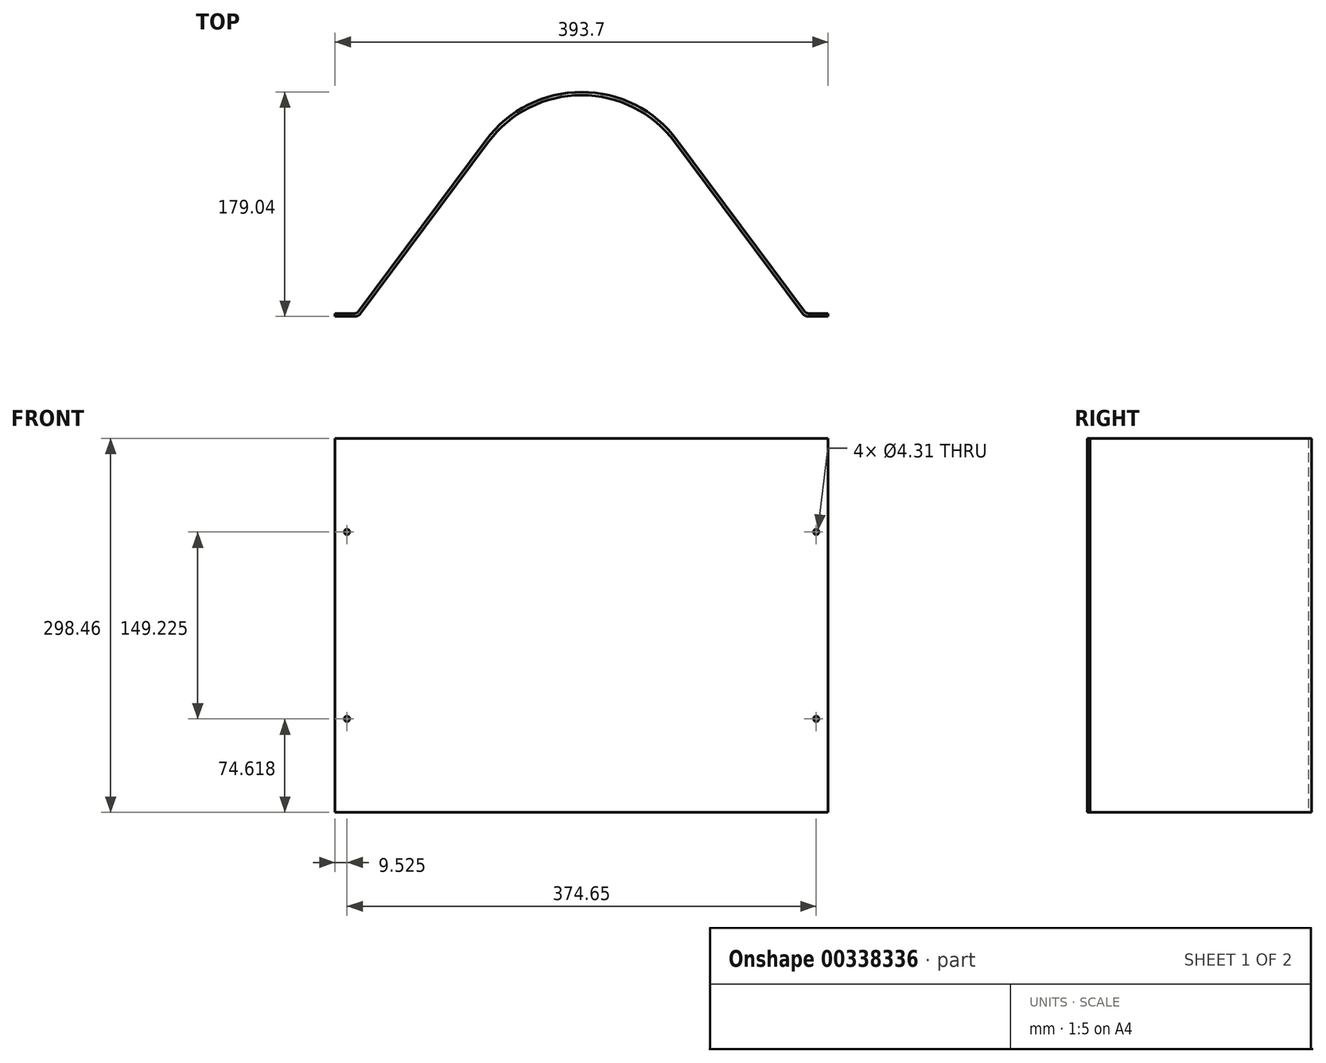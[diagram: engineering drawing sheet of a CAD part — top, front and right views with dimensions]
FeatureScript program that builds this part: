
annotation { "Feature Type Name" : "Feature", "Feature Type Description" : "" }
export const myFeature = defineFeature(function(context is Context, id is Id, definition is map)
    precondition{}
    {
        {
            var Q0;
            Q0=qCreatedBy(makeId("Top.planeOp"),FACE);
            var sketch = newSketch(context, id + "F0", { "sketchPlane" : qUnion([Q0])});
            skLineSegment(sketch, "E0", {"start": v(0, 0) * mm, "end": v(15.88, 0) * mm});
            skLineSegment(sketch, "E1", {"start": v(0, 0) * mm, "end": v(0, -2.38) * mm});
            skLineSegment(sketch, "E2", {"start": v(0, -2.38) * mm, "end": v(393.7, -2.38) * mm});
            skArc(sketch, "E3", {"start": v(15.88, 0) * mm, "mid": v(17.3, 0.34) * mm, "end": v(18.42, 1.28) * mm});
            skLineSegment(sketch, "E4", {"start": v(393.7, -2.38) * mm, "end": v(393.7, 0) * mm});
            skLineSegment(sketch, "E5", {"start": v(393.7, 0) * mm, "end": v(377.83, 0) * mm});
            skLineSegment(sketch, "E6", {"start": v(196.85, -2.38) * mm, "end": v(196.85, 81.57) * mm, "construction": true});
            skArc(sketch, "E7", {"start": v(375.28, 1.28) * mm, "mid": v(376.4, 0.34) * mm, "end": v(377.83, 0) * mm});
            skArc(sketch, "E8", {"start": v(273.1, 138.39) * mm, "mid": v(196.85, 176.66) * mm, "end": v(120.6, 138.39) * mm});
            skLineSegment(sketch, "E9", {"start": v(273.1, 138.39) * mm, "end": v(375.28, 1.28) * mm});
            skLineSegment(sketch, "E10", {"start": v(120.6, 138.39) * mm, "end": v(18.42, 1.28) * mm});
            skSolve(sketch);
        }
        {
            var Q0;
            Q0 = qSketchRegion(id + "F0", true);
            extrude(context, id + "F1", {"entities" : qUnion([Q0]), "depth" : 609.6 * mm});
        }
        {
            var Q0;
            Q0=makeQuery(id+"F1.opExtrude","SWEPT_FACE",FACE,{"disambiguationData":[OSD([sQuery(id+"F0.wireOp",EDGE,"E2")])]});
            shell(context, id + "F2", {"entities" : qUnion([Q0]), "thickness" : 2.38 * mm});
        }
        {
            var Q0;
            Q0=makeQuery(id+"F1.opExtrude","SWEPT_FACE",FACE,{"disambiguationData":[OSD([sQuery(id+"F0.wireOp",EDGE,"E2")])]});
            var sketch = newSketch(context, id + "F3", { "sketchPlane" : qUnion([Q0])});
            skLineSegment(sketch, "E11.bottom", {"start": v(0, 609.6) * mm, "end": v(393.7, 609.6) * mm});
            skLineSegment(sketch, "E11.top", {"start": v(0, 454.03) * mm, "end": v(393.7, 454.03) * mm});
            skLineSegment(sketch, "E11.left", {"start": v(0, 609.6) * mm, "end": v(0, 454.03) * mm});
            skLineSegment(sketch, "E11.right", {"start": v(393.7, 609.6) * mm, "end": v(393.7, 454.03) * mm});
            skLineSegment(sketch, "E12.bottom", {"start": v(393.7, 0) * mm, "end": v(0, 0) * mm});
            skLineSegment(sketch, "E12.top", {"start": v(393.7, 155.57) * mm, "end": v(0, 155.57) * mm});
            skLineSegment(sketch, "E12.left", {"start": v(393.7, 0) * mm, "end": v(393.7, 155.57) * mm});
            skLineSegment(sketch, "E12.right", {"start": v(0, 0) * mm, "end": v(0, 155.57) * mm});
            skLineSegment(sketch, "E13", {"start": v(196.85, 454.03) * mm, "end": v(196.85, 155.57) * mm, "construction": true});
            skSolve(sketch);
        }
        {
            var Q0;
            Q0 = qSketchRegion(id + "F3", true);
            var Q1;
            Q1=makeQuery(id+"F1.opExtrude","SWEPT_FACE",FACE,{"disambiguationData":[OSD([sQuery(id+"F0.wireOp",EDGE,"E10")])]});
            extrude(context, id + "F4", {"entities" : qUnion([Q0]), "operationType" : NewBodyOperationType.REMOVE, "endBound" : BoundingType.THROUGH_ALL, "oppositeDirection" : true, "endBoundEntityFace" : qUnion([Q1]), "depth" : 25.4 * mm});
        }
        {
            var Q0;
            Q0=makeQuery(id+"F4.boolean.opBoolean","SPLIT",FACE,{"disambiguationData":[TD([makeQuery(id+"F1.opExtrude","SWEPT_FACE",FACE,{"disambiguationData":[OSD([sQuery(id+"F0.wireOp",EDGE,"E4")])]})])],"derivedFrom":makeQuery(id+"F1.opExtrude","SWEPT_FACE",FACE,{"disambiguationData":[OSD([sQuery(id+"F0.wireOp",EDGE,"E2")])]})});
            var sketch = newSketch(context, id + "F5", { "sketchPlane" : qUnion([Q0])});
            skLineSegment(sketch, "E14", {"start": v(384.18, 454.03) * mm, "end": v(384.18, 379.41) * mm, "construction": true});
            skLineSegment(sketch, "E15", {"start": v(384.18, 379.41) * mm, "end": v(384.18, 304.8) * mm, "construction": true});
            skLineSegment(sketch, "E16", {"start": v(384.18, 304.8) * mm, "end": v(384.18, 230.19) * mm, "construction": true});
            skLineSegment(sketch, "E17", {"start": v(384.18, 230.19) * mm, "end": v(384.18, 155.57) * mm, "construction": true});
            skCircle(sketch, "E18", {"center": v(384.18, 230.19) * mm, "radius": 2.15 * mm});
            skCircle(sketch, "E19", {"center": v(384.18, 379.41) * mm, "radius": 2.15 * mm});
            skLineSegment(sketch, "E20", {"start": v(384.18, 304.8) * mm, "end": v(393.7, 304.8) * mm, "construction": true});
            skLineSegment(sketch, "E21", {"start": v(196.85, 454.03) * mm, "end": v(196.85, 155.58) * mm, "construction": true});
            skLineSegment(sketch, "E22", {"start": v(0, 304.8) * mm, "end": v(9.53, 304.8) * mm, "construction": true});
            skLineSegment(sketch, "E23", {"start": v(9.53, 304.8) * mm, "end": v(9.53, 379.41) * mm, "construction": true});
            skLineSegment(sketch, "E24", {"start": v(9.53, 304.8) * mm, "end": v(9.53, 230.19) * mm, "construction": true});
            skCircle(sketch, "E25", {"center": v(9.53, 379.41) * mm, "radius": 2.15 * mm});
            skCircle(sketch, "E26", {"center": v(9.53, 230.19) * mm, "radius": 2.15 * mm});
            skSolve(sketch);
        }
        {
            var Q0;
            Q0 = qSketchRegion(id + "F5", true);
            var Q1;
            Q1=makeQuery(id+"F1.opExtrude","SWEPT_FACE",FACE,{"disambiguationData":[OSD([sQuery(id+"F0.wireOp",EDGE,"E5")])]});
            extrude(context, id + "F6", {"entities" : qUnion([Q0]), "operationType" : NewBodyOperationType.REMOVE, "endBound" : BoundingType.UP_TO_SURFACE, "oppositeDirection" : true, "endBoundEntityFace" : qUnion([Q1]), "depth" : 25.4 * mm});
        }
    });
